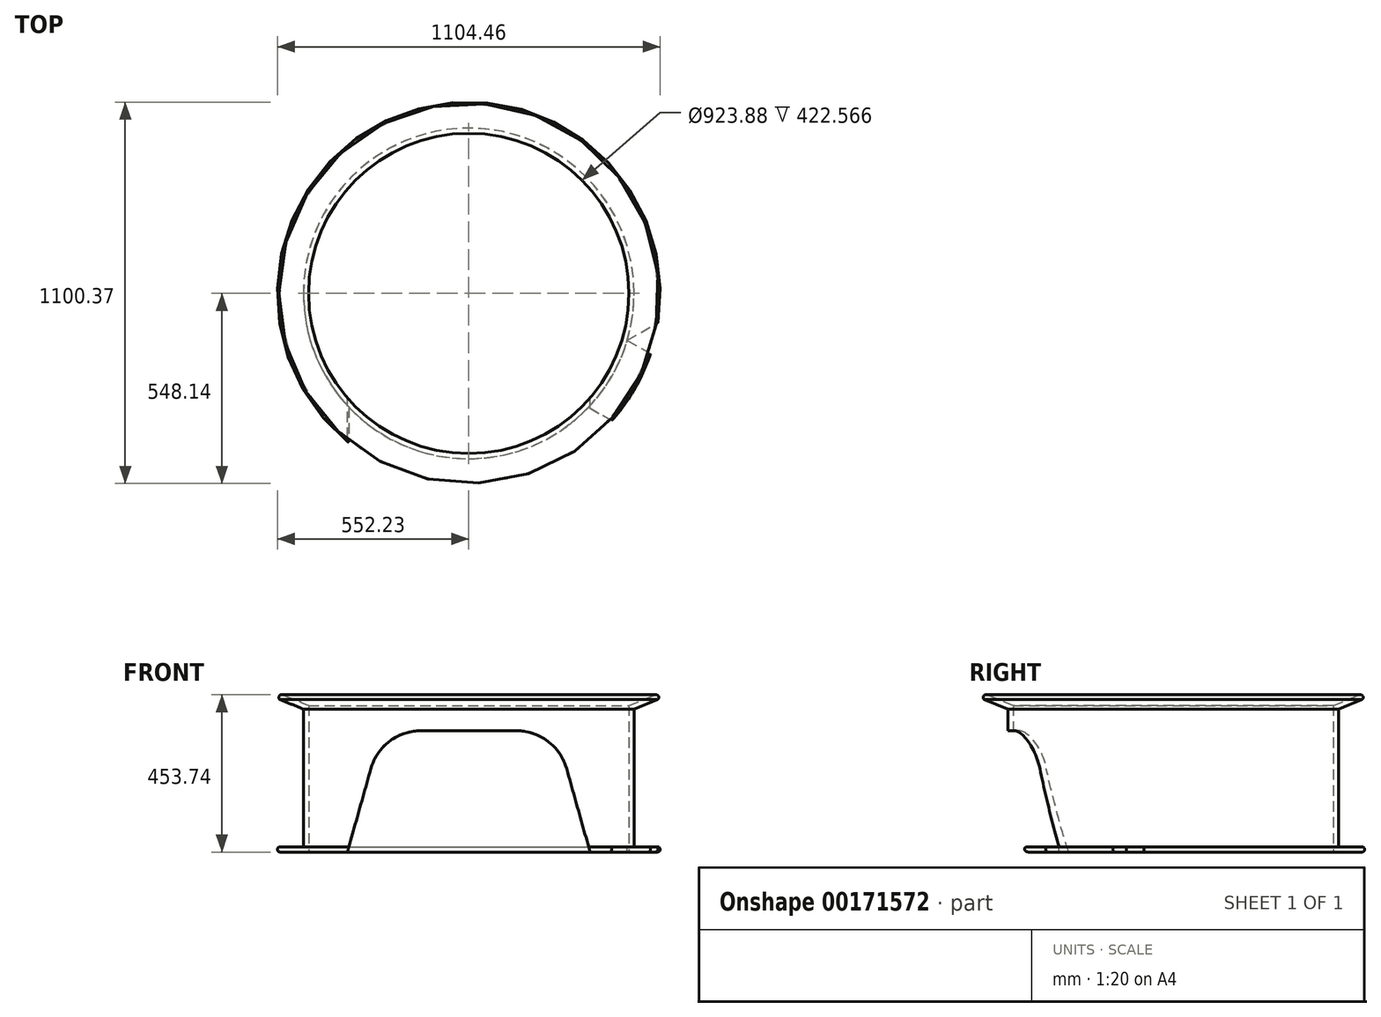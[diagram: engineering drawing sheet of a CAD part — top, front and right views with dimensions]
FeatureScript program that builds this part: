
annotation { "Feature Type Name" : "Feature", "Feature Type Description" : "" }
export const myFeature = defineFeature(function(context is Context, id is Id, definition is map)
    precondition{}
    {
        {
            var Q0;
            Q0=qCreatedBy(makeId("Front.planeOp"),FACE);
            var sketch = newSketch(context, id + "F0", { "sketchPlane" : qUnion([Q0])});
            skLineSegment(sketch, "E0", {"start": v(0, 0) * mm, "end": v(544.73, 0) * mm});
            skArc(sketch, "E1", {"start": v(544.73, 0) * mm, "mid": v(552.23, 7.5) * mm, "end": v(544.73, 15) * mm});
            skLineSegment(sketch, "E2", {"start": v(544.73, 15) * mm, "end": v(476.94, 15) * mm});
            skLineSegment(sketch, "E3", {"start": v(476.94, 15) * mm, "end": v(476.94, 412.45) * mm});
            skLineSegment(sketch, "E4", {"start": v(476.94, 412.45) * mm, "end": v(544.73, 439.84) * mm});
            skLineSegment(sketch, "E5", {"start": v(0, 0) * mm, "end": v(0, 456.67) * mm});
            skPoint(sketch, "E6.orphan", {"position": v(-544.27, 0) * mm});
            skLineSegment(sketch, "E7", {"start": v(537.73, 453.19) * mm, "end": v(461.94, 422.57) * mm});
            skLineSegment(sketch, "E8", {"start": v(461.94, 422.57) * mm, "end": v(461.94, 0) * mm});
            skLineSegment(sketch, "E9", {"start": v(461.94, 0) * mm, "end": v(544.73, 0) * mm});
            skLineSegment(sketch, "E10", {"start": v(544.73, 439.84) * mm, "end": v(537.73, 453.19) * mm, "construction": true});
            skArc(sketch, "E11", {"start": v(544.73, 439.84) * mm, "mid": v(547.28, 449.68) * mm, "end": v(537.73, 453.19) * mm});
            skSolve(sketch);
        }
        {
            var Q0;
            Q0 = qSketchRegion(id + "F0", true);
            var Q1;
            Q1=sQuery(id+"F0.wireOp",EDGE,"E5");
            revolve(context, id + "F1", {"entities" : qUnion([Q0]), "axis" : qUnion([Q1]), "revolveType" : RevolveType.FULL});
        }
        {
            var Q0;
            Q0=qCreatedBy(makeId("Front.planeOp"),FACE);
            var sketch = newSketch(context, id + "F2", { "sketchPlane" : qUnion([Q0])});
            skLineSegment(sketch, "E12", {"start": v(-350, 0) * mm, "end": v(350, 0) * mm});
            skLineSegment(sketch, "E13", {"start": v(-350, 0) * mm, "end": v(-282.26, 240.65) * mm});
            skArc(sketch, "E14", {"start": v(-137.87, 350) * mm, "mid": v(-228.43, 319.58) * mm, "end": v(-282.26, 240.65) * mm});
            skLineSegment(sketch, "E15", {"start": v(-137.87, 350) * mm, "end": v(0, 350) * mm});
            skLineSegment(sketch, "E16", {"start": v(0, 350) * mm, "end": v(0, 0) * mm, "construction": true});
            skLineSegment(sketch, "E17.MirrorCS", {"start": v(137.87, 350) * mm, "end": v(0, 350) * mm});
            skArc(sketch, "E18.MirrorCS", {"start": v(137.87, 350) * mm, "mid": v(228.43, 319.58) * mm, "end": v(282.26, 240.65) * mm});
            skLineSegment(sketch, "E19.MirrorCS", {"start": v(350, 0) * mm, "end": v(282.26, 240.65) * mm});
            skSolve(sketch);
        }
        {
            var Q0;
            Q0 = qSketchRegion(id + "F2", true);
            extrude(context, id + "F3", {"entities" : qUnion([Q0]), "operationType" : NewBodyOperationType.REMOVE, "depth" : 557 * mm});
        }
        {
            var Q0;
            {var subQ3=makeQuery(id+"F3.boolean.opBoolean","COPY",FACE,{"derivedFrom":makeQuery(id+"F3.opExtrude","SWEPT_FACE",FACE,{"disambiguationData":[OSD([sQuery(id+"F2.wireOp",EDGE,"E19.MirrorCS")])]})});Q0=makeQuery(id+"FboyLu5mt41KeWR_1.2.F3.boolean.opBoolean","SPLIT",FACE,{"disambiguationData":[TD([subQ3])],"derivedFrom":makeQuery(id+"FboyLu5mt41KeWR_1.1.F3.boolean.opBoolean","SPLIT",FACE,{"disambiguationData":[TD([subQ3])],"derivedFrom":makeQuery(id+"F1.opRevolve","SWEPT_FACE",FACE,{"disambiguationData":[OSD([sQuery(id+"F0.wireOp",EDGE,"E2")])]})})});}
            var sketch = newSketch(context, id + "F4", { "sketchPlane" : qUnion([Q0])});
            skLineSegment(sketch, "E20.0", {"start": v(345.78, -328.5) * mm, "end": v(345.78, -420.92) * mm});
            skLineSegment(sketch, "E21", {"start": v(457.37, -135.2) * mm, "end": v(528.6, -176.33) * mm});
            skLineSegment(sketch, "E22", {"start": v(345.78, -328.5) * mm, "end": v(417, -369.61) * mm});
            skPoint(sketch, "E23.0.end.orphan", {"position": v(537.41, -89) * mm});
            skArc(sketch, "E24", {"start": v(347.89, -428.87) * mm, "mid": v(478.25, -276.12) * mm, "end": v(545.36, -86.84) * mm, "construction": true});
            skArc(sketch, "E25.0", {"start": v(345.78, -436.97) * mm, "mid": v(382.87, -404.86) * mm, "end": v(417, -369.61) * mm});
            skLineSegment(sketch, "E26", {"start": v(457.37, -135.2) * mm, "end": v(551.32, -80.97) * mm});
            skLineSegment(sketch, "E27", {"start": v(345.78, -420.92) * mm, "end": v(345.78, -436.97) * mm});
            skArc(sketch, "E28.trimOffspring", {"start": v(528.6, -176.33) * mm, "mid": v(542.06, -129.15) * mm, "end": v(551.32, -80.97) * mm});
            skSolve(sketch);
        }
        {
            var Q0;
            Q0 = qSketchRegion(id + "F4", true);
            extrude(context, id + "F5", {"entities" : qUnion([Q0]), "operationType" : NewBodyOperationType.REMOVE, "oppositeDirection" : true, "depth" : 15 * mm});
        }
    });
